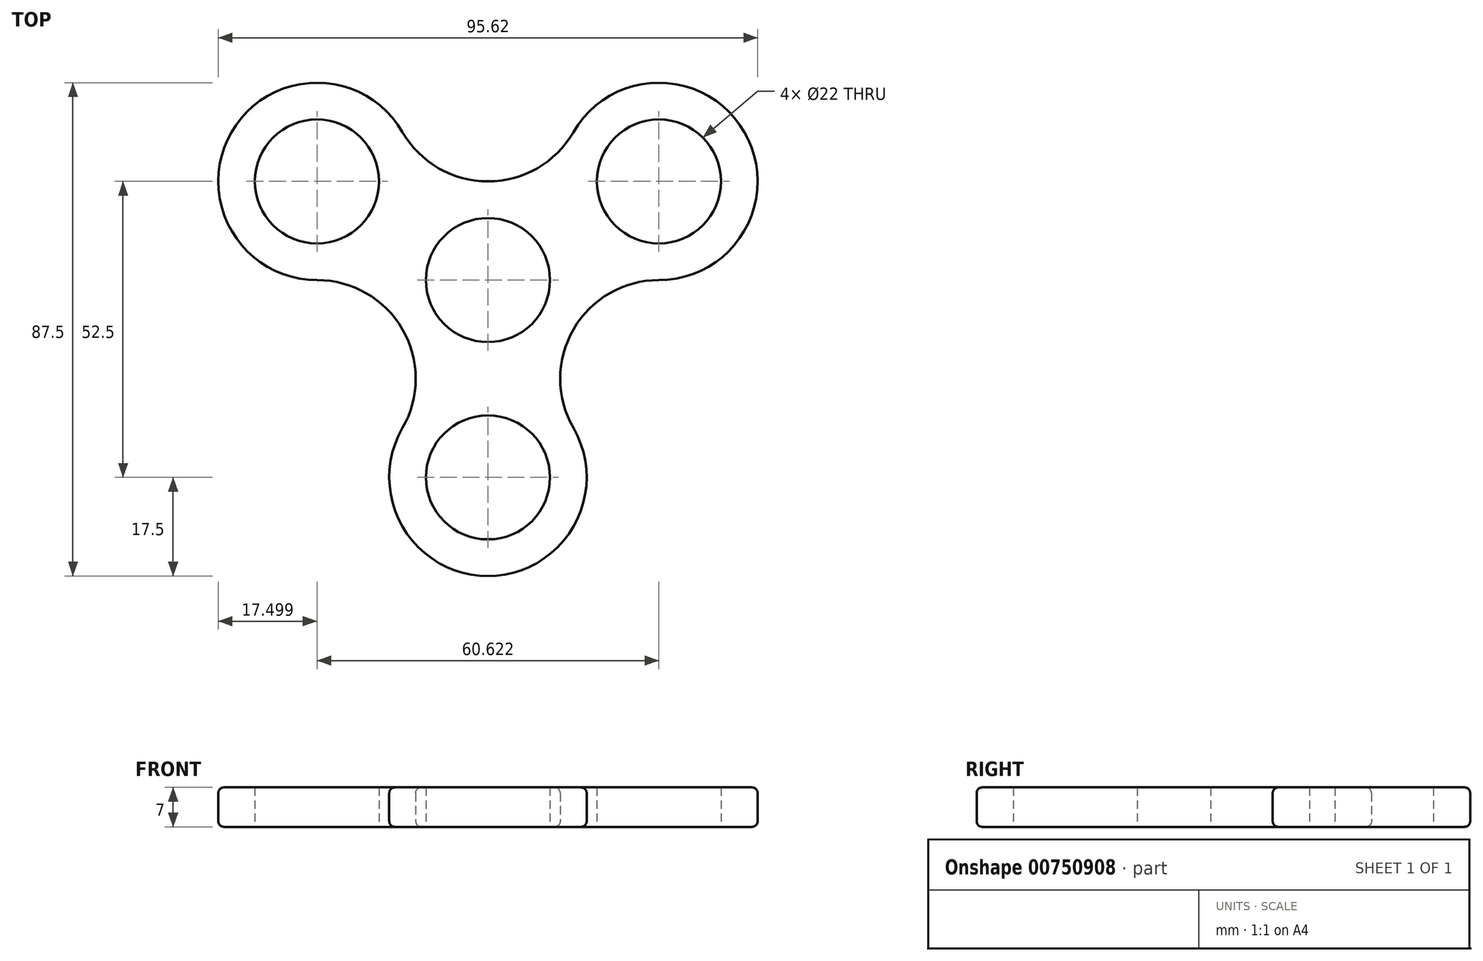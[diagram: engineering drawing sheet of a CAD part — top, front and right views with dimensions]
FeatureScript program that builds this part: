
annotation { "Feature Type Name" : "Feature", "Feature Type Description" : "" }
export const myFeature = defineFeature(function(context is Context, id is Id, definition is map)
    precondition{}
    {
        {
            var Q0;
            Q0=qCreatedBy(makeId("Top.planeOp"),FACE);
            var sketch = newSketch(context, id + "F0", { "sketchPlane" : qUnion([Q0])});
            skCircle(sketch, "E0", {"center": v(0, 0) * mm, "radius": 11 * mm});
            skCircle(sketch, "E1", {"center": v(0, 0) * mm, "radius": 4 * mm});
            skSolve(sketch);
        }
        {
            var Q0;
            Q0=qCreatedBy(makeId("Top.planeOp"),FACE);
            var sketch = newSketch(context, id + "F1", { "sketchPlane" : qUnion([Q0])});
            skArc(sketch, "E2", {"start": v(-15.16, -26.25) * mm, "mid": v(0, -52.5) * mm, "end": v(15.16, -26.25) * mm});
            skArc(sketch, "E3.1.0", {"start": v(30.31, 0) * mm, "mid": v(45.47, 26.25) * mm, "end": v(15.16, 26.25) * mm});
            skArc(sketch, "E3.2.0", {"start": v(-15.16, 26.25) * mm, "mid": v(-45.47, 26.25) * mm, "end": v(-30.31, 0) * mm});
            skPoint(sketch, "E3.center", {"position": v(0, 0) * mm});
            skArc(sketch, "E4", {"start": v(-15.16, -26.25) * mm, "mid": v(-15.16, -8.75) * mm, "end": v(-30.31, 0) * mm});
            skArc(sketch, "E5.1.0", {"start": v(30.31, 0) * mm, "mid": v(15.16, -8.75) * mm, "end": v(15.16, -26.25) * mm});
            skArc(sketch, "E5.2.0", {"start": v(-15.16, 26.25) * mm, "mid": v(0, 17.5) * mm, "end": v(15.16, 26.25) * mm});
            skCircle(sketch, "E6", {"center": v(0, -35) * mm, "radius": 11 * mm});
            skCircle(sketch, "E7.1.0", {"center": v(30.31, 17.5) * mm, "radius": 11 * mm});
            skCircle(sketch, "E7.2.0", {"center": v(-30.31, 17.5) * mm, "radius": 11 * mm});
            skCircle(sketch, "E8", {"center": v(0, 0) * mm, "radius": 11 * mm});
            skSolve(sketch);
        }
        {
            var Q0;
            Q0=makeQuery(id+"F1.imprint","IMPRINT",FACE,{"disambiguationData":[TD([[makeQuery(id+"F1.imprint","IMPRINT",EDGE,{"derivedFrom":sQuery(id+"F1.wireOp",EDGE,"E2")}),1.0]])]});
            extrude(context, id + "F2", {"entities" : qUnion([Q0]), "endBound" : BoundingType.SYMMETRIC, "depth" : 7 * mm, "offsetDistance" : 25 * mm});
        }
        {
            var Q0;
            Q0=makeQuery(id+"F2.opExtrude","CAP_EDGE",EDGE,{"disambiguationData":[OSD([sQuery(id+"F1.wireOp",EDGE,"E4")])],"isStart":false});
            var Q1;
            Q1=makeQuery(id+"F2.opExtrude","CAP_EDGE",EDGE,{"disambiguationData":[OSD([sQuery(id+"F1.wireOp",EDGE,"E2")])],"isStart":true});
            fillet(context, id + "F3", {"entities" : qUnion([Q0, Q1]), "radius" : 1 * mm, "tangentPropagation" : true, "allowEdgeOverflow" : false});
        }
    });
